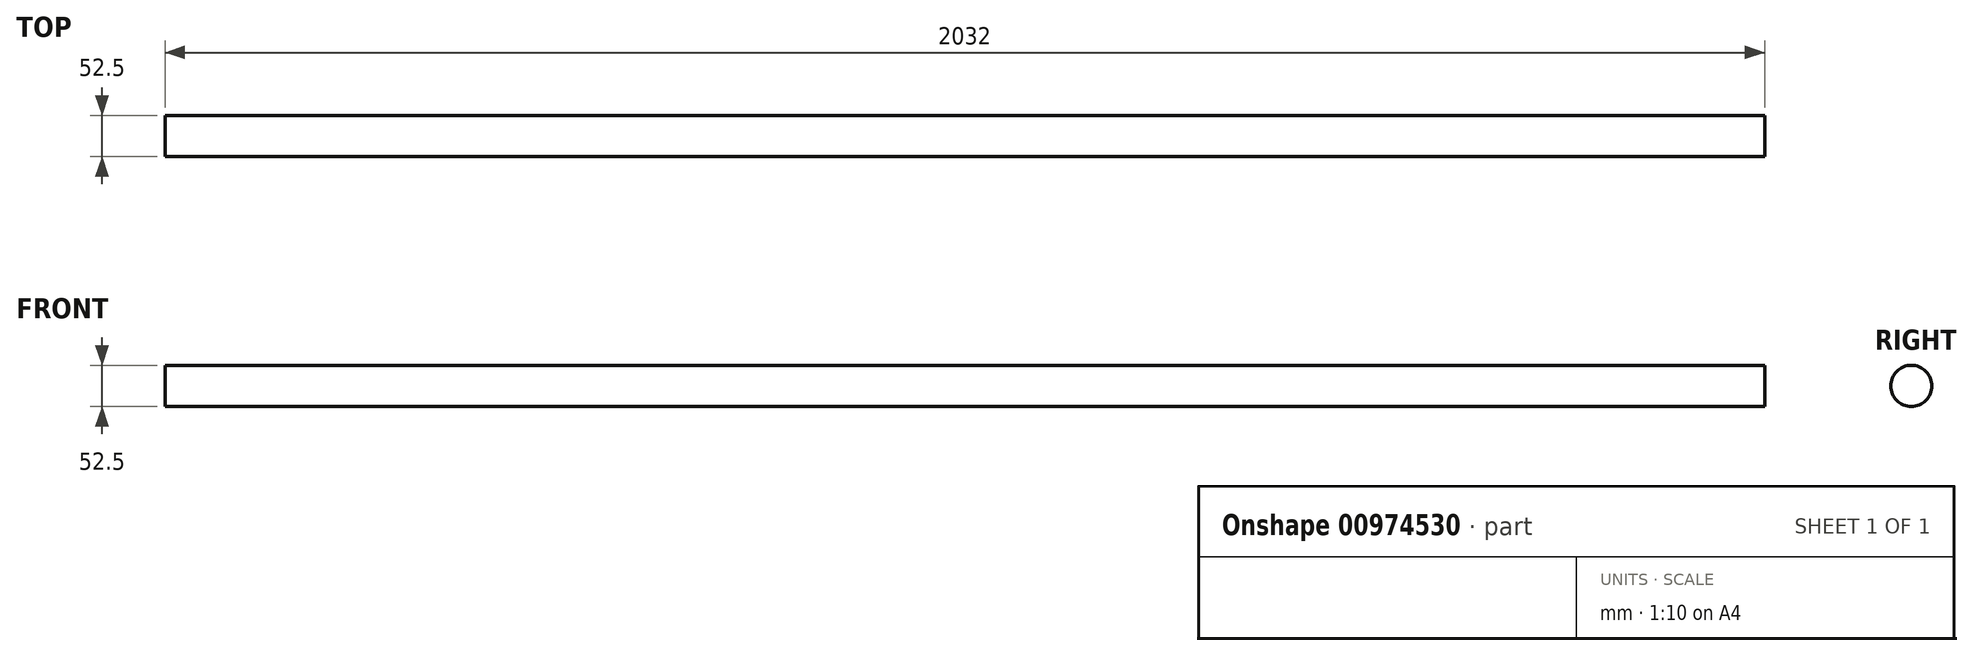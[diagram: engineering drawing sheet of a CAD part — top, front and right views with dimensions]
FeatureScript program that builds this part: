
annotation { "Feature Type Name" : "Feature", "Feature Type Description" : "" }
export const myFeature = defineFeature(function(context is Context, id is Id, definition is map)
    precondition{}
    {
        {
            var Q0;
            Q0=qCreatedBy(makeId("Right.planeOp"),FACE);
            var sketch = newSketch(context, id + "F0", { "sketchPlane" : qUnion([Q0])});
            skCircle(sketch, "E0", {"center": v(0, 0) * mm, "radius": 26.25 * mm});
            skSolve(sketch);
        }
        {
            var Q0;
            Q0=qSketchRegion(id+"F0",true);
            extrude(context, id + "F1", {"entities" : qUnion([Q0]), "flatOperationType" : FlatOperationType.REMOVE, "oppositeDirection" : true, "depth" : 2032 * mm, "offsetDistance" : 25.4 * mm, "domain" : OperationDomain.MODEL, "symmetric" : true});
        }
    });
